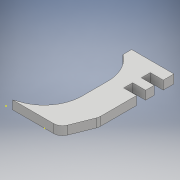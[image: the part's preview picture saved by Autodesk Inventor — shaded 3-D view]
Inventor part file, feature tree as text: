
AUTODESK INVENTOR PART (.ipt)
format: ipt  version: 2017 (Build 210142000, 142)  size: 150,016 bytes
history: native  units: mm
features: sketch x5, extrude x2, hole x1
ambient origin geometry x8: Origin, YZ Plane, XZ Plane, XY Plane, X Axis, Y Axis, Z Axis, Center Point
bodies: Solid1 (feature_tree)
feature tree (8):
  sketch  "Sketch1"  dims[d0=22.0mm d1=90.0deg]
  sketch  "Sketch2"  dims[d2=0.0mm d3=15.0mm]
  extrude  "Extrusion1"  TaperAngle=90.0deg  [1 undecoded]
  hole  "Hole1"  [1 undecoded]
  sketch  "Sketch4"  dims[d6=22.0mm]
  extrude  "Extrusion2"  Depth=13.0mm
  sketch  "Sketch3"  dims[d4=0.0mm d5=13.0mm]
  sketch  "Sketch5"  dims[d7=12.0mm d8=22.5mm d9=15.0mm d10=90.0mm d11=37.0mm d12=5.0mm d13=12.124057mm d14=5.2mm d15=5.2mm d16=5.0mm d17=7.5mm d18=5.0mm d19=0.0mm d20=23.0mm d21=7.5mm d22=7.5mm d23=3.5mm d24=3.4mm d25=6.0mm d26=4.0mm d27=2.0mm d28=90.0deg d29=8.0mm d30=20.594885mm d31=7.0mm d32=40.0mm d33=0.0mm]
note: 2 required parameter values undecoded (feature->parameter linkage not recoverable at this tier; creation-order binding heuristic only, values carry confidence <= 0.55)
